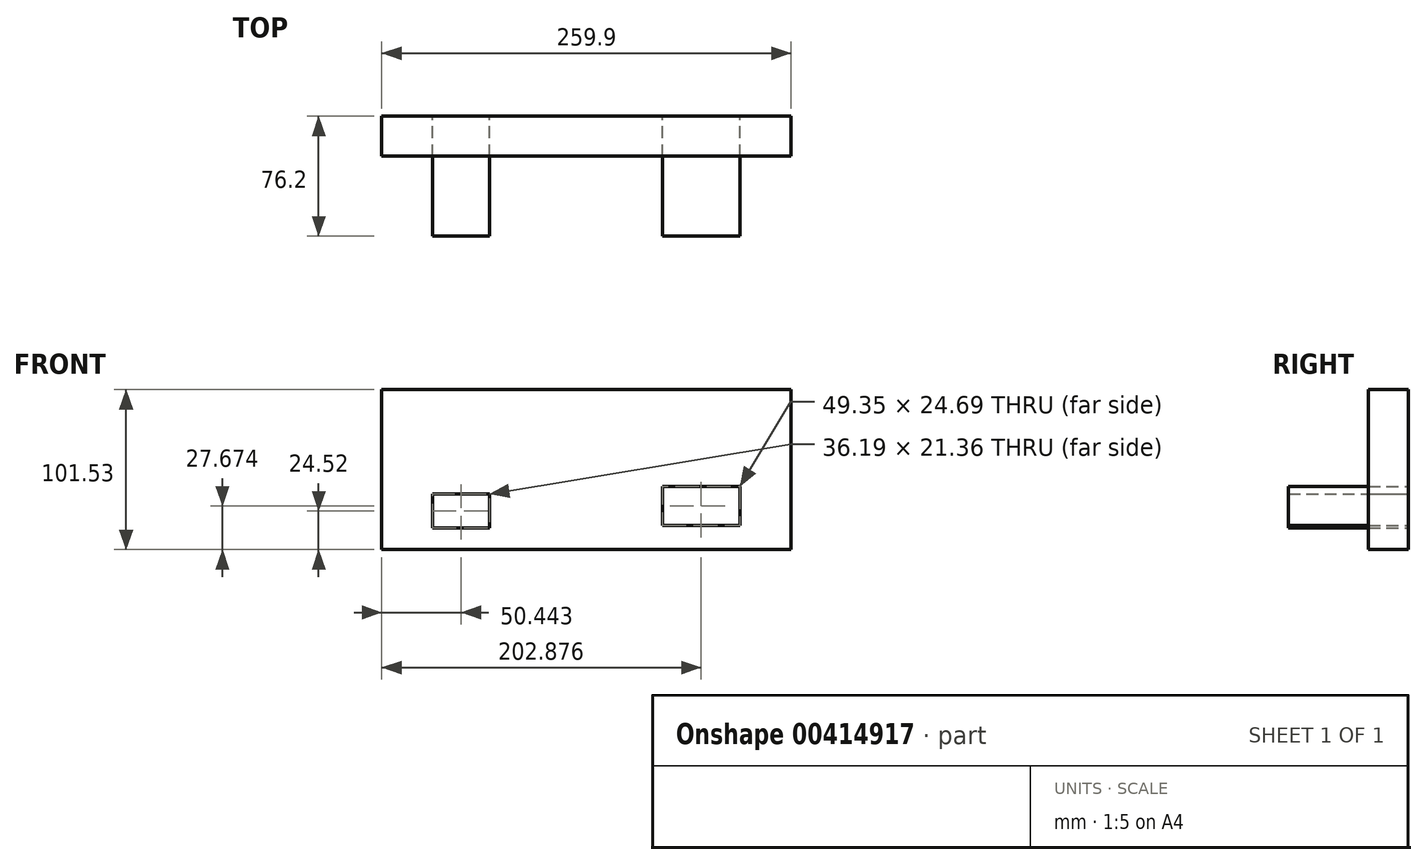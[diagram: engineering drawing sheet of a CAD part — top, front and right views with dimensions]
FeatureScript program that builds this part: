
annotation { "Feature Type Name" : "Feature", "Feature Type Description" : "" }
export const myFeature = defineFeature(function(context is Context, id is Id, definition is map)
    precondition{}
    {
        {
            var Q0;
            Q0=qCreatedBy(makeId("Front.planeOp"),FACE);
            var sketch = newSketch(context, id + "F0", { "sketchPlane" : qUnion([Q0])});
            skLineSegment(sketch, "E0.bottom", {"start": v(-103.63, 40.82) * mm, "end": v(156.27, 40.82) * mm});
            skLineSegment(sketch, "E0.top", {"start": v(-103.63, -60.71) * mm, "end": v(156.27, -60.71) * mm});
            skLineSegment(sketch, "E0.left", {"start": v(-103.63, 40.82) * mm, "end": v(-103.63, -60.71) * mm});
            skLineSegment(sketch, "E0.right", {"start": v(156.27, 40.82) * mm, "end": v(156.27, -60.71) * mm});
            skLineSegment(sketch, "E1.bottom", {"start": v(-71.28, -25.51) * mm, "end": v(-35.1, -25.51) * mm});
            skLineSegment(sketch, "E1.top", {"start": v(-71.28, -46.87) * mm, "end": v(-35.1, -46.87) * mm});
            skLineSegment(sketch, "E1.left", {"start": v(-71.28, -25.51) * mm, "end": v(-71.28, -46.87) * mm});
            skLineSegment(sketch, "E1.right", {"start": v(-35.1, -25.51) * mm, "end": v(-35.1, -46.87) * mm});
            skLineSegment(sketch, "E2.bottom", {"start": v(74.57, -20.7) * mm, "end": v(123.92, -20.7) * mm});
            skLineSegment(sketch, "E2.top", {"start": v(74.57, -45.38) * mm, "end": v(123.92, -45.38) * mm});
            skLineSegment(sketch, "E2.left", {"start": v(74.57, -20.7) * mm, "end": v(74.57, -45.38) * mm});
            skLineSegment(sketch, "E2.right", {"start": v(123.92, -20.7) * mm, "end": v(123.92, -45.38) * mm});
            skSolve(sketch);
        }
        {
            var Q0;
            Q0=makeQuery(id+"F0.imprint","IMPRINT",FACE,{"disambiguationData":[TD([[makeQuery(id+"F0.imprint","IMPRINT",EDGE,{"derivedFrom":sQuery(id+"F0.wireOp",EDGE,"E1.bottom")}),-1.0]])]});
            var Q1;
            Q1=makeQuery(id+"F0.imprint","IMPRINT",FACE,{"disambiguationData":[TD([[makeQuery(id+"F0.imprint","IMPRINT",EDGE,{"derivedFrom":sQuery(id+"F0.wireOp",EDGE,"E2.bottom")}),-1.0]])]});
            extrude(context, id + "F1", {"entities" : qUnion([Q0, Q1]), "depth" : 76.2 * mm});
        }
        {
            var Q0;
            Q0=makeQuery(id+"F0.imprint","IMPRINT",FACE,{"disambiguationData":[TD([[makeQuery(id+"F0.imprint","IMPRINT",EDGE,{"derivedFrom":sQuery(id+"F0.wireOp",EDGE,"E0.bottom")}),-1.0]])]});
            extrude(context, id + "F2", {"entities" : qUnion([Q0]), "depth" : 25.4 * mm});
        }
    });
